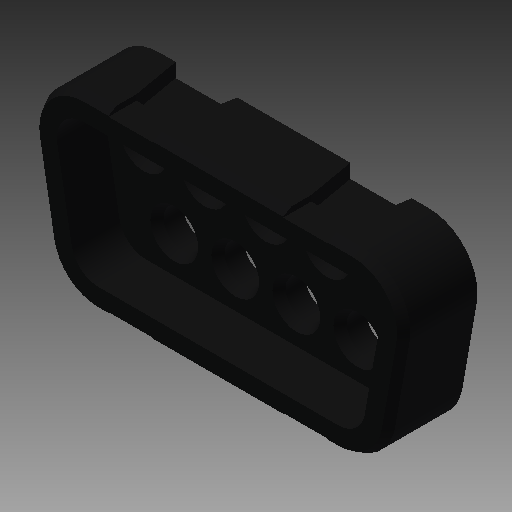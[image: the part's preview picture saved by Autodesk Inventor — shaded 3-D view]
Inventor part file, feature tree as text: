
AUTODESK INVENTOR PART (.ipt)
format: ipt  version: 2017 (Build 210142000, 142)  size: 201,216 bytes
history: native  units: in
note: dims shown in document units (in); Inventor stores cm internally (conversion verified against a paired STEP export)
features: chamfer x1
ambient origin geometry x8: Origin, YZ Plane, XZ Plane, XY Plane, X Axis, Y Axis, Z Axis, Center Point
bodies: Solid1 (feature_tree)
feature tree (1):
  chamfer  "Chamfer2"  [1 undecoded]
note: 1 required parameter value undecoded (feature->parameter linkage not recoverable at this tier; creation-order binding heuristic only, values carry confidence <= 0.55)
